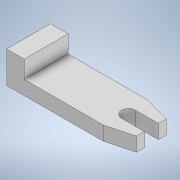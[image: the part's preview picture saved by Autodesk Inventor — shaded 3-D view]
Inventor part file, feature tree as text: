
AUTODESK INVENTOR PART (.ipt)
format: ipt  version: 2021 (Build 250183000, 183)  size: 117,760 bytes
history: native  units: mm
features: extrude x2, chamfer x2, sketch x2, other x1
ambient origin geometry x8: Origin, YZ Plane, XZ Plane, XY Plane, X Axis, Y Axis, Z Axis, Center Point
bodies: Body1 (feature_tree)
feature tree (7):
  other  "Sólido1"
  extrude  "Extrusão1"  Depth=10.0mm
  extrude  "Extrusão2"  Depth=70.0mm
  chamfer  "Chanfro1"  Distance=25.0mm
  chamfer  "Chanfro2"  Distance=4.0mm
  sketch  "Esboço1"  dims[d0=18.0mm d1=10.0mm]
  sketch  "Esboço2"  dims[d2=8.0mm d3=70.0mm d4=25.0mm d5=0.0mm d6=4.0mm d7=13.0mm d8=10.0mm d9=0.0mm d10=4.0mm d11=2.0mm d12=105.0deg d13=4.0mm d14=2.0mm d15=105.0deg]
